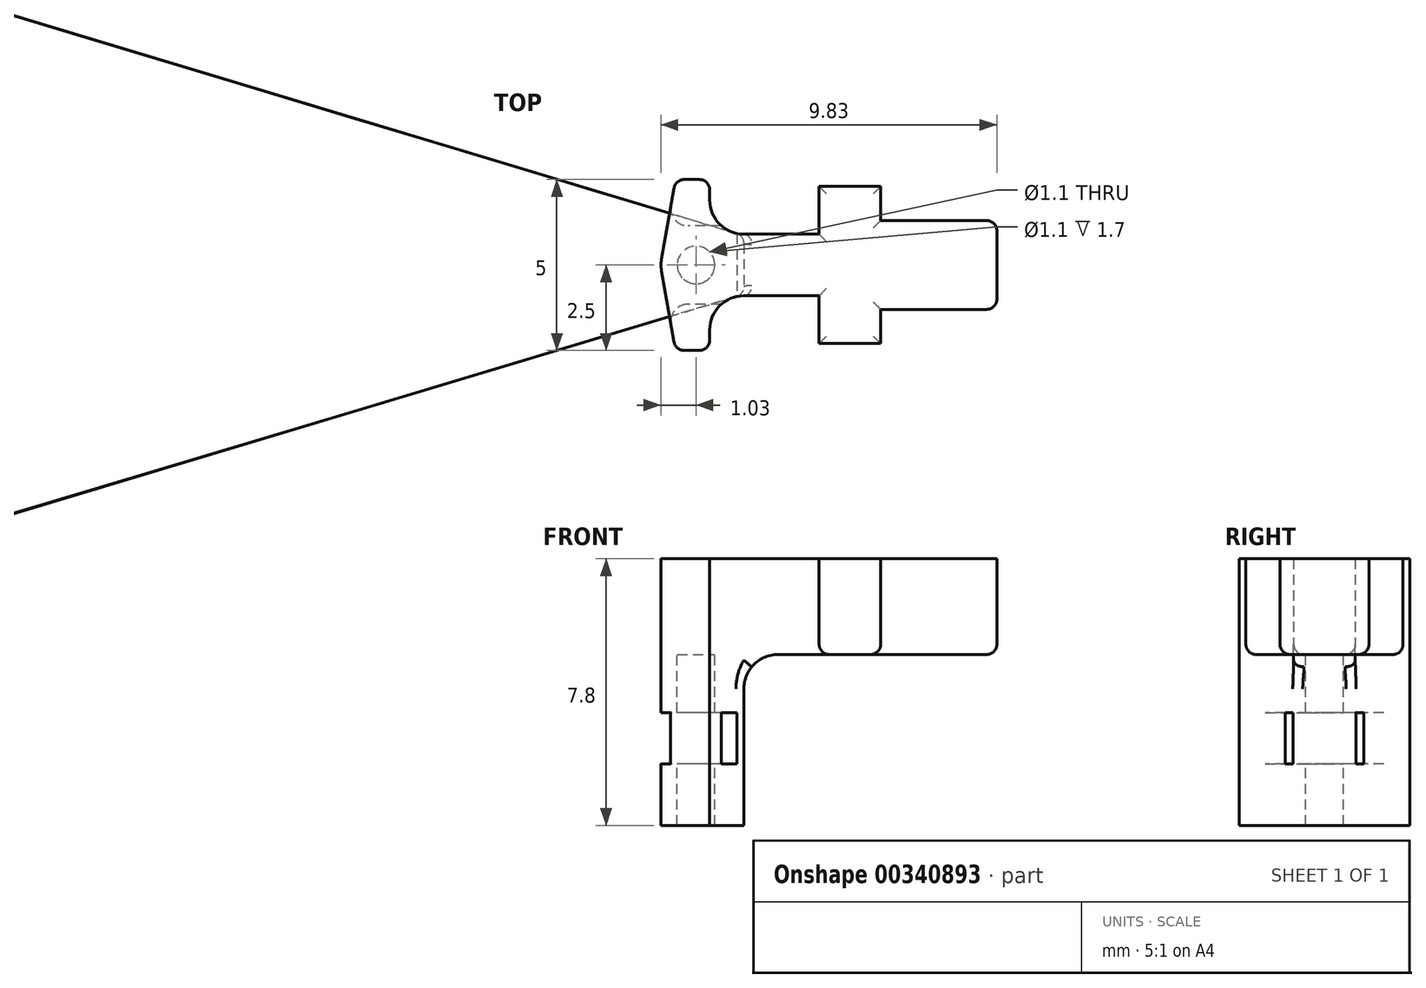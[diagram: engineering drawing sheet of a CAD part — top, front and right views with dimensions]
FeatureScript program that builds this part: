
annotation { "Feature Type Name" : "Feature", "Feature Type Description" : "" }
export const myFeature = defineFeature(function(context is Context, id is Id, definition is map)
    precondition{}
    {
        {
            var Q0;
            Q0=qCreatedBy(makeId("Top.planeOp"),FACE);
            var sketch = newSketch(context, id + "F0", { "sketchPlane" : qUnion([Q0])});
            skLineSegment(sketch, "E0", {"start": v(-3.2, -2.5) * mm, "end": v(-3.2, -1.9) * mm});
            skLineSegment(sketch, "E1", {"start": v(-2.2, -0.9) * mm, "end": v(0, -0.9) * mm});
            skLineSegment(sketch, "E2", {"start": v(0, -0.9) * mm, "end": v(0, -2.3) * mm});
            skLineSegment(sketch, "E3", {"start": v(0, -2.3) * mm, "end": v(1.8, -2.3) * mm});
            skLineSegment(sketch, "E4", {"start": v(1.8, -2.3) * mm, "end": v(1.8, -1.3) * mm});
            skLineSegment(sketch, "E5", {"start": v(1.8, -1.3) * mm, "end": v(5.2, -1.3) * mm});
            skLineSegment(sketch, "E6", {"start": v(5.2, -1.3) * mm, "end": v(5.2, 0) * mm});
            skLineSegment(sketch, "E7", {"start": v(-3.2, -2.5) * mm, "end": v(-4.2, -2.5) * mm});
            skLineSegment(sketch, "E8", {"start": v(-4.2, -2.5) * mm, "end": v(-4.64, 0) * mm});
            skPoint(sketch, "E9.visualSharp", {"position": v(-3.2, -0.9) * mm});
            skArc(sketch, "E9.filletArc", {"start": v(-2.2, -0.9) * mm, "mid": v(-2.9, -1.2) * mm, "end": v(-3.2, -1.9) * mm});
            skLineSegment(sketch, "E10.MirrorCS", {"start": v(1.8, 2.3) * mm, "end": v(1.8, 1.3) * mm});
            skArc(sketch, "E11.MirrorCS", {"start": v(-2.2, 0.9) * mm, "mid": v(-2.9, 1.2) * mm, "end": v(-3.2, 1.9) * mm});
            skLineSegment(sketch, "E12.MirrorCS", {"start": v(-3.2, 2.5) * mm, "end": v(-3.2, 1.9) * mm});
            skLineSegment(sketch, "E13.MirrorCS", {"start": v(1.8, 1.3) * mm, "end": v(5.2, 1.3) * mm});
            skLineSegment(sketch, "E14.MirrorCS", {"start": v(5.2, 1.3) * mm, "end": v(5.2, 0) * mm});
            skLineSegment(sketch, "E15.MirrorCS", {"start": v(-3.2, 2.5) * mm, "end": v(-4.2, 2.5) * mm});
            skLineSegment(sketch, "E16.MirrorCS", {"start": v(0, 0.9) * mm, "end": v(0, 2.3) * mm});
            skPoint(sketch, "E17.MirrorP", {"position": v(-3.2, 0.9) * mm});
            skLineSegment(sketch, "E18.MirrorCS", {"start": v(-2.2, 0.9) * mm, "end": v(0, 0.9) * mm});
            skLineSegment(sketch, "E19.MirrorCS", {"start": v(0, 2.3) * mm, "end": v(1.8, 2.3) * mm});
            skLineSegment(sketch, "E20.MirrorCS", {"start": v(-4.2, 2.5) * mm, "end": v(-4.64, 0) * mm});
            skSolve(sketch);
        }
        {
            var Q0;
            Q0 = qSketchRegion(id + "F0", true);
            extrude(context, id + "F1", {"entities" : qUnion([Q0]), "depth" : 2.8 * mm});
        }
        {
            var Q0;
            Q0=makeQuery(id+"F1.opExtrude","CAP_FACE",FACE,{"disambiguationData":[OSD([sQuery(id+"F0.wireOp",EDGE,"E0"),sQuery(id+"F0.wireOp",EDGE,"E1"),sQuery(id+"F0.wireOp",EDGE,"E2"),sQuery(id+"F0.wireOp",EDGE,"E3"),sQuery(id+"F0.wireOp",EDGE,"E4"),sQuery(id+"F0.wireOp",EDGE,"E5"),sQuery(id+"F0.wireOp",EDGE,"E6"),sQuery(id+"F0.wireOp",EDGE,"E7"),sQuery(id+"F0.wireOp",EDGE,"E8"),sQuery(id+"F0.wireOp",EDGE,"E9.filletArc"),sQuery(id+"F0.wireOp",EDGE,"E10.MirrorCS"),sQuery(id+"F0.wireOp",EDGE,"E11.MirrorCS"),sQuery(id+"F0.wireOp",EDGE,"E12.MirrorCS"),sQuery(id+"F0.wireOp",EDGE,"E13.MirrorCS"),sQuery(id+"F0.wireOp",EDGE,"E14.MirrorCS"),sQuery(id+"F0.wireOp",EDGE,"E15.MirrorCS"),sQuery(id+"F0.wireOp",EDGE,"E16.MirrorCS"),sQuery(id+"F0.wireOp",EDGE,"E18.MirrorCS"),sQuery(id+"F0.wireOp",EDGE,"E19.MirrorCS"),sQuery(id+"F0.wireOp",EDGE,"E20.MirrorCS")])],"isStart":true});
            var sketch = newSketch(context, id + "F2", { "sketchPlane" : qUnion([Q0])});
            skLineSegment(sketch, "E21.0", {"start": v(-3.2, -2.5) * mm, "end": v(-4.2, -2.5) * mm});
            skLineSegment(sketch, "E22.0", {"start": v(-4.2, -2.5) * mm, "end": v(-4.64, 0) * mm});
            skLineSegment(sketch, "E23.0", {"start": v(-3.2, -2.5) * mm, "end": v(-3.2, -1.9) * mm});
            skLineSegment(sketch, "E24.0", {"start": v(-3.2, 2.5) * mm, "end": v(-4.2, 2.5) * mm});
            skLineSegment(sketch, "E25.0", {"start": v(-4.2, 2.5) * mm, "end": v(-4.64, 0) * mm});
            skPoint(sketch, "E25.1", {"position": v(-2.9, -1.2) * mm});
            skLineSegment(sketch, "E26", {"start": v(-2.2, -0.9) * mm, "end": v(-2.2, 0.9) * mm});
            skArc(sketch, "E27.0", {"start": v(-2.2, -0.9) * mm, "mid": v(-2.9, -1.2) * mm, "end": v(-3.2, -1.9) * mm});
            skArc(sketch, "E28.0", {"start": v(-2.2, 0.9) * mm, "mid": v(-2.9, 1.2) * mm, "end": v(-3.2, 1.9) * mm});
            skLineSegment(sketch, "E29.0", {"start": v(-3.2, 2.5) * mm, "end": v(-3.2, 1.9) * mm});
            skCircle(sketch, "E30", {"center": v(-3.6, 0) * mm, "radius": 0.55 * mm});
            skSolve(sketch);
        }
        {
            var Q0;
            Q0 = qSketchRegion(id + "F2", true);
            extrude(context, id + "F3", {"entities" : qUnion([Q0]), "operationType" : NewBodyOperationType.ADD, "depth" : 5 * mm});
        }
        {
            var Q0;
            Q0=makeQuery(id+"F3.opExtrude","CAP_EDGE",EDGE,{"disambiguationData":[OSD([sQuery(id+"F2.wireOp",EDGE,"E26")])],"isStart":true});
            var Q1;
            Q1=makeQuery(id+"F3.boolean.opBoolean","MERGE",EDGE,{"derivedFrom":[makeQuery(id+"F1.opExtrude","SWEPT_EDGE",EDGE,{"disambiguationData":[OSD([sQuery(id+"F0.wireOp",EDGE,"E8"),sQuery(id+"F0.wireOp",EDGE,"E20.MirrorCS")])]}),makeQuery(id+"F3.opExtrude","SWEPT_EDGE",EDGE,{"disambiguationData":[OSD([sQuery(id+"F2.wireOp",EDGE,"E22.0"),sQuery(id+"F2.wireOp",EDGE,"E25.0")])]})]});
            fillet(context, id + "F4", {"entities" : qUnion([Q0, Q1]), "radius" : 1 * mm, "tangentPropagation" : true, "allowEdgeOverflow" : false});
        }
        {
            var Q0;
            Q0=makeQuery(id+"F1.opExtrude","SWEPT_EDGE",EDGE,{"disambiguationData":[OSD([sQuery(id+"F0.wireOp",EDGE,"E5"),sQuery(id+"F0.wireOp",EDGE,"E6")])]});
            var Q1;
            Q1=makeQuery(id+"F1.opExtrude","SWEPT_EDGE",EDGE,{"disambiguationData":[OSD([sQuery(id+"F0.wireOp",EDGE,"E13.MirrorCS"),sQuery(id+"F0.wireOp",EDGE,"E14.MirrorCS")])]});
            var Q2;
            Q2=makeQuery(id+"F3.boolean.opBoolean","MERGE",EDGE,{"derivedFrom":[makeQuery(id+"F1.opExtrude","SWEPT_EDGE",EDGE,{"disambiguationData":[OSD([sQuery(id+"F0.wireOp",EDGE,"E12.MirrorCS"),sQuery(id+"F0.wireOp",EDGE,"E15.MirrorCS")])]}),makeQuery(id+"F3.opExtrude","SWEPT_EDGE",EDGE,{"disambiguationData":[OSD([sQuery(id+"F2.wireOp",EDGE,"E21.0"),sQuery(id+"F2.wireOp",EDGE,"E23.0")])]})]});
            var Q3;
            Q3=makeQuery(id+"F3.boolean.opBoolean","MERGE",EDGE,{"derivedFrom":[makeQuery(id+"F1.opExtrude","SWEPT_EDGE",EDGE,{"disambiguationData":[OSD([sQuery(id+"F0.wireOp",EDGE,"E15.MirrorCS"),sQuery(id+"F0.wireOp",EDGE,"E20.MirrorCS")])]}),makeQuery(id+"F3.opExtrude","SWEPT_EDGE",EDGE,{"disambiguationData":[OSD([sQuery(id+"F2.wireOp",EDGE,"E21.0"),sQuery(id+"F2.wireOp",EDGE,"E22.0")])]})]});
            var Q4;
            Q4=makeQuery(id+"F3.boolean.opBoolean","MERGE",EDGE,{"derivedFrom":[makeQuery(id+"F1.opExtrude","SWEPT_EDGE",EDGE,{"disambiguationData":[OSD([sQuery(id+"F0.wireOp",EDGE,"E0"),sQuery(id+"F0.wireOp",EDGE,"E7")])]}),makeQuery(id+"F3.opExtrude","SWEPT_EDGE",EDGE,{"disambiguationData":[OSD([sQuery(id+"F2.wireOp",EDGE,"E24.0"),sQuery(id+"F2.wireOp",EDGE,"E29.0")])]})]});
            var Q5;
            Q5=makeQuery(id+"F3.boolean.opBoolean","MERGE",EDGE,{"derivedFrom":[makeQuery(id+"F1.opExtrude","SWEPT_EDGE",EDGE,{"disambiguationData":[OSD([sQuery(id+"F0.wireOp",EDGE,"E7"),sQuery(id+"F0.wireOp",EDGE,"E8")])]}),makeQuery(id+"F3.opExtrude","SWEPT_EDGE",EDGE,{"disambiguationData":[OSD([sQuery(id+"F2.wireOp",EDGE,"E24.0"),sQuery(id+"F2.wireOp",EDGE,"E25.0")])]})]});
            var Q6;
            {var subQ0=sQuery(id+"F0.wireOp",EDGE,"E11.MirrorCS");var subQ1=sQuery(id+"F0.wireOp",EDGE,"E10.MirrorCS");var subQ2=sQuery(id+"F0.wireOp",EDGE,"E9.filletArc");var subQ3=sQuery(id+"F0.wireOp",EDGE,"E14.MirrorCS");var subQ4=sQuery(id+"F0.wireOp",EDGE,"E6");var subQ5=sQuery(id+"F0.wireOp",EDGE,"E5");var subQ6=sQuery(id+"F0.wireOp",EDGE,"E1");var subQ7=sQuery(id+"F0.wireOp",EDGE,"E13.MirrorCS");var subQ8=sQuery(id+"F0.wireOp",EDGE,"E2");var subQ9=sQuery(id+"F0.wireOp",EDGE,"E3");var subQ10=sQuery(id+"F0.wireOp",EDGE,"E4");var subQ11=sQuery(id+"F0.wireOp",EDGE,"E16.MirrorCS");var subQ12=sQuery(id+"F0.wireOp",EDGE,"E18.MirrorCS");var subQ13=sQuery(id+"F0.wireOp",EDGE,"E19.MirrorCS");Q6=makeQuery(id+"F3.boolean.opBoolean","SPLIT",FACE,{"disambiguationData":[TD([makeQuery(id+"F1.opExtrude","SWEPT_FACE",FACE,{"disambiguationData":[OSD([subQ6])]})])],"derivedFrom":makeQuery(id+"F1.opExtrude","CAP_FACE",FACE,{"disambiguationData":[OSD([sQuery(id+"F0.wireOp",EDGE,"E0"),subQ6,subQ8,subQ9,subQ10,subQ5,subQ4,sQuery(id+"F0.wireOp",EDGE,"E7"),sQuery(id+"F0.wireOp",EDGE,"E8"),subQ2,subQ1,subQ0,sQuery(id+"F0.wireOp",EDGE,"E12.MirrorCS"),subQ7,subQ3,sQuery(id+"F0.wireOp",EDGE,"E15.MirrorCS"),subQ11,subQ12,subQ13,sQuery(id+"F0.wireOp",EDGE,"E20.MirrorCS")])],"isStart":true})});}
            fillet(context, id + "F5", {"entities" : qUnion([Q0, Q1, Q2, Q3, Q4, Q5, Q6]), "radius" : .3 * mm, "tangentPropagation" : true, "allowEdgeOverflow" : false});
        }
        {
            var Q0;
            Q0=makeQuery(id+"F0.imprint","IMPRINT",FACE,{"disambiguationData":[TD([[makeQuery(id+"F0.imprint","IMPRINT",EDGE,{"derivedFrom":sQuery(id+"F0.wireOp",EDGE,"E0")}),1.0]])]});
            cPlane(context, id + "F6", {"entities" : qUnion([Q0]), "cplaneType" : CPlaneType.OFFSET, "offset" : 3.2 * mm, "oppositeDirection" : true, "width" : 150 * mm, "height" : 150 * mm});
        }
        {
            var Q0;
            Q0=qCreatedBy(id+"F6.planeOp",FACE);
            var sketch = newSketch(context, id + "F7", { "sketchPlane" : qUnion([Q0])});
            skLineSegment(sketch, "E31.bottom", {"start": v(-2.4, 1.15) * mm, "end": v(-5, 1.15) * mm});
            skLineSegment(sketch, "E31.top", {"start": v(-2.4, -1.15) * mm, "end": v(-5, -1.15) * mm});
            skLineSegment(sketch, "E31.left", {"start": v(-2.4, 1.15) * mm, "end": v(-2.4, -1.15) * mm});
            skLineSegment(sketch, "E31.right", {"start": v(-5, 1.15) * mm, "end": v(-5, -1.15) * mm});
            skCircle(sketch, "E32.0", {"center": v(-3.6, 0) * mm, "radius": 0.55 * mm, "construction": true});
            skSolve(sketch);
        }
        {
            var Q0;
            Q0 = qSketchRegion(id + "F7", true);
            extrude(context, id + "F8", {"entities" : qUnion([Q0]), "operationType" : NewBodyOperationType.REMOVE, "depth" : 1.5 * mm});
        }
        {
            var Q0;
            Q0=makeQuery(id+"F8.boolean.opBoolean","INTERSECT",EDGE,{"derivedFrom":[makeQuery(id+"F3.boolean.opBoolean","MERGE",FACE,{"derivedFrom":[makeQuery(id+"F1.opExtrude","SWEPT_FACE",FACE,{"disambiguationData":[OSD([sQuery(id+"F0.wireOp",EDGE,"E20.MirrorCS")])]}),makeQuery(id+"F3.opExtrude","SWEPT_FACE",FACE,{"disambiguationData":[OSD([sQuery(id+"F2.wireOp",EDGE,"E22.0")])]})]}),makeQuery(id+"F8.opExtrude","SWEPT_FACE",FACE,{"disambiguationData":[OSD([sQuery(id+"F7.wireOp",EDGE,"E31.bottom")])]})]});
            var Q1;
            Q1=makeQuery(id+"F8.boolean.opBoolean","INTERSECT",EDGE,{"derivedFrom":[makeQuery(id+"F3.boolean.opBoolean","MERGE",FACE,{"derivedFrom":[makeQuery(id+"F1.opExtrude","SWEPT_FACE",FACE,{"disambiguationData":[OSD([sQuery(id+"F0.wireOp",EDGE,"E8")])]}),makeQuery(id+"F3.opExtrude","SWEPT_FACE",FACE,{"disambiguationData":[OSD([sQuery(id+"F2.wireOp",EDGE,"E25.0")])]})]}),makeQuery(id+"F8.opExtrude","SWEPT_FACE",FACE,{"disambiguationData":[OSD([sQuery(id+"F7.wireOp",EDGE,"E31.top")])]})]});
            fillet(context, id + "F9", {"entities" : qUnion([Q0, Q1]), "radius" : .5 * mm, "tangentPropagation" : true, "allowEdgeOverflow" : false});
        }
    });
